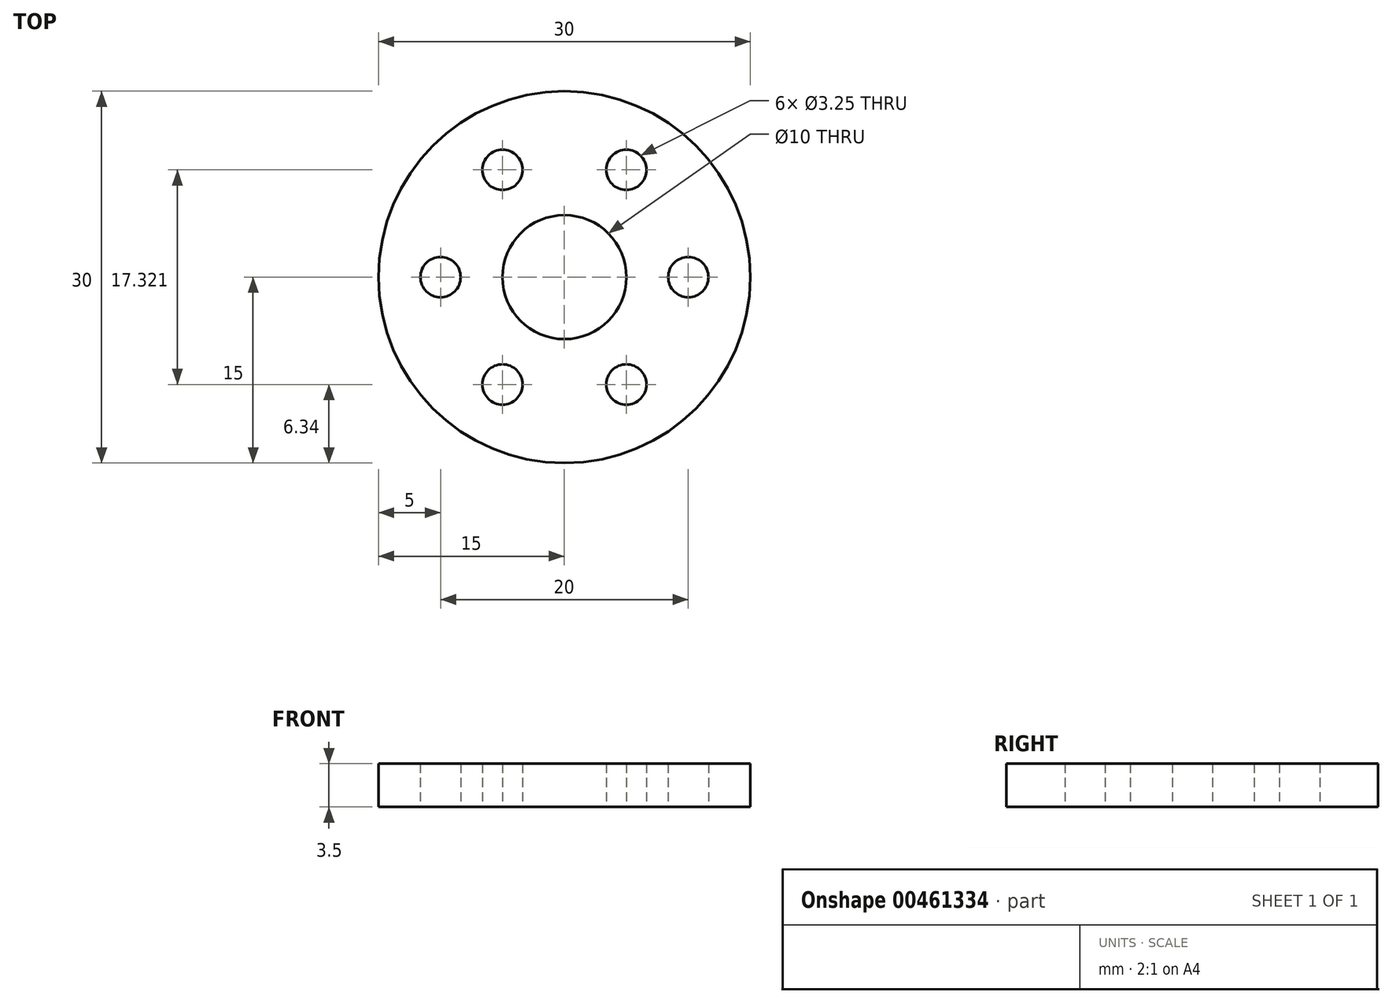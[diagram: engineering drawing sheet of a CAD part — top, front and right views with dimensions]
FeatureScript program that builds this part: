
annotation { "Feature Type Name" : "Feature", "Feature Type Description" : "" }
export const myFeature = defineFeature(function(context is Context, id is Id, definition is map)
    precondition{}
    {
        {
            var Q0;
            Q0=qCreatedBy(makeId("Top.planeOp"),FACE);
            var sketch = newSketch(context, id + "F0", { "sketchPlane" : qUnion([Q0])});
            skCircle(sketch, "E0", {"center": v(0, 0) * mm, "radius": 5 * mm});
            skCircle(sketch, "E1", {"center": v(0, 0) * mm, "radius": 15 * mm});
            skCircle(sketch, "E2", {"center": v(10, 0) * mm, "radius": 1.63 * mm});
            skCircle(sketch, "E3.1.0", {"center": v(5, 8.66) * mm, "radius": 1.63 * mm});
            skCircle(sketch, "E3.2.0", {"center": v(-5, 8.66) * mm, "radius": 1.63 * mm});
            skCircle(sketch, "E3.3.0", {"center": v(-10, 0) * mm, "radius": 1.63 * mm});
            skCircle(sketch, "E3.4.0", {"center": v(-5, -8.66) * mm, "radius": 1.63 * mm});
            skCircle(sketch, "E3.5.0", {"center": v(5, -8.66) * mm, "radius": 1.63 * mm});
            skSolve(sketch);
        }
        {
            var Q0;
            Q0=makeQuery(id+"F0.imprint","IMPRINT",FACE,{"disambiguationData":[TD([[makeQuery(id+"F0.imprint","IMPRINT",EDGE,{"derivedFrom":sQuery(id+"F0.wireOp",EDGE,"E0")}),-1.0]])]});
            extrude(context, id + "F1", {"entities" : qUnion([Q0]), "depth" : 3.5 * mm});
        }
    });
